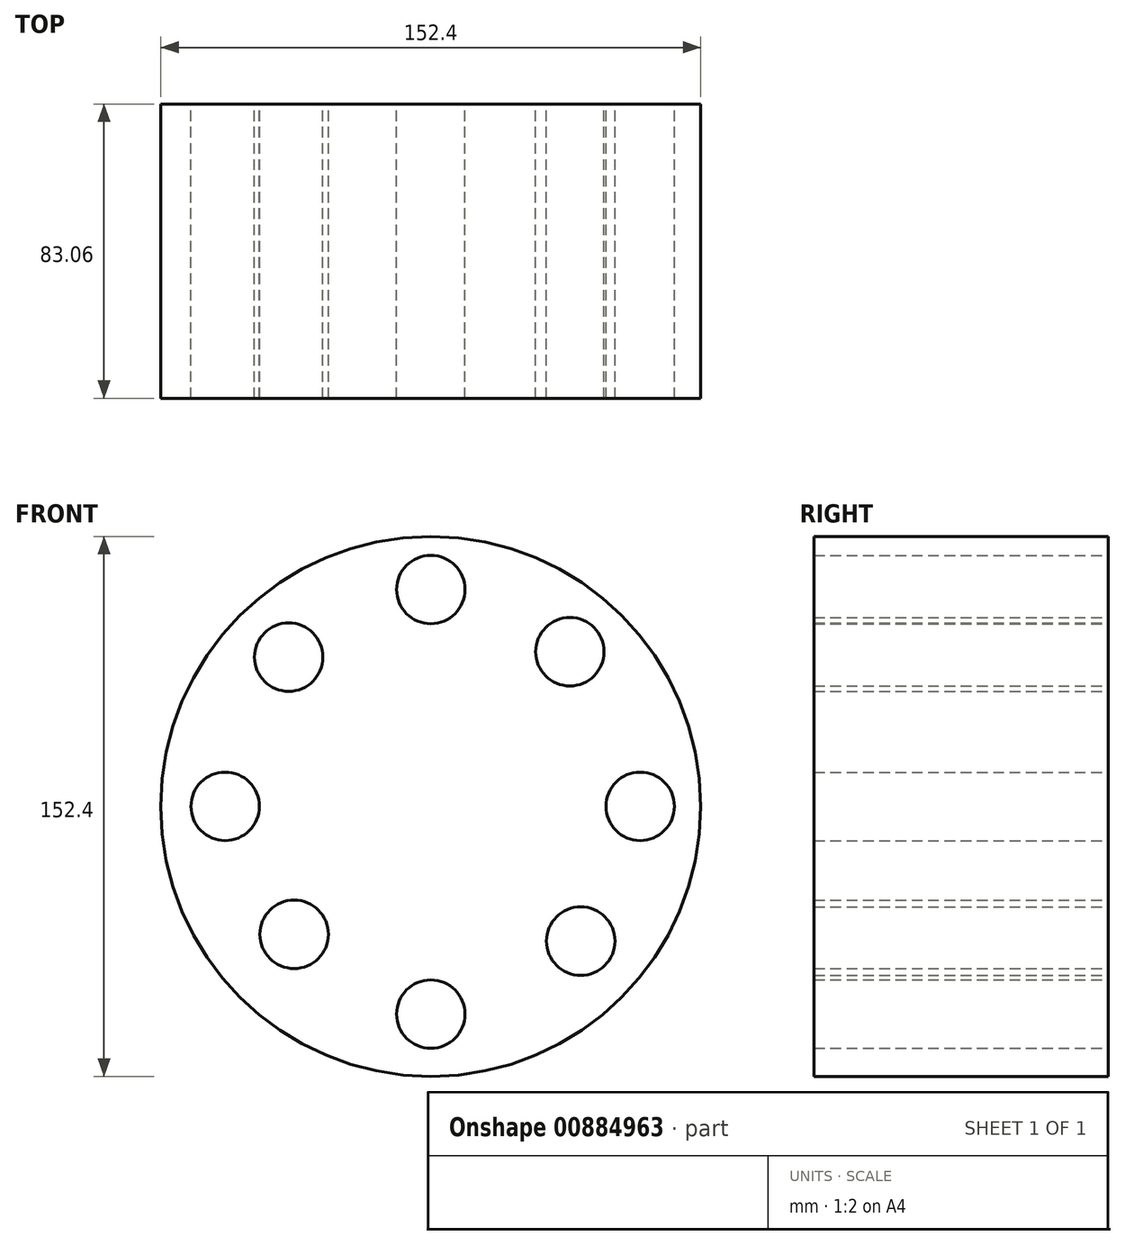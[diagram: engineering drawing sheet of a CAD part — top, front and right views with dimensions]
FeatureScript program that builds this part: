
annotation { "Feature Type Name" : "Feature", "Feature Type Description" : "" }
export const myFeature = defineFeature(function(context is Context, id is Id, definition is map)
    precondition{}
    {
        {
            var Q0;
            Q0=qCreatedBy(makeId("Front.planeOp"),FACE);
            var sketch = newSketch(context, id + "F0", { "sketchPlane" : qUnion([Q0])});
            skCircle(sketch, "E0", {"center": v(0, 0) * mm, "radius": 76.2 * mm});
            skCircle(sketch, "E1", {"center": v(-40.11, 42.12) * mm, "radius": 9.66 * mm});
            skCircle(sketch, "E2", {"center": v(0, 61.2) * mm, "radius": 9.66 * mm});
            skCircle(sketch, "E3", {"center": v(39.26, 43.64) * mm, "radius": 9.66 * mm});
            skCircle(sketch, "E4", {"center": v(59.1, 0) * mm, "radius": 9.66 * mm});
            skCircle(sketch, "E5", {"center": v(-58.05, 0) * mm, "radius": 9.66 * mm});
            skCircle(sketch, "E6", {"center": v(-38.59, -36.11) * mm, "radius": 9.66 * mm});
            skCircle(sketch, "E7", {"center": v(42.32, -38.02) * mm, "radius": 9.66 * mm});
            skCircle(sketch, "E8", {"center": v(0, -58.63) * mm, "radius": 9.66 * mm});
            skSolve(sketch);
        }
        {
            var Q0;
            Q0 = qSketchRegion(id + "F0", true);
            extrude(context, id + "F1", {"entities" : qUnion([Q0]), "depth" : 83.06 * mm, "offsetDistance" : 25.4 * mm});
        }
    });
